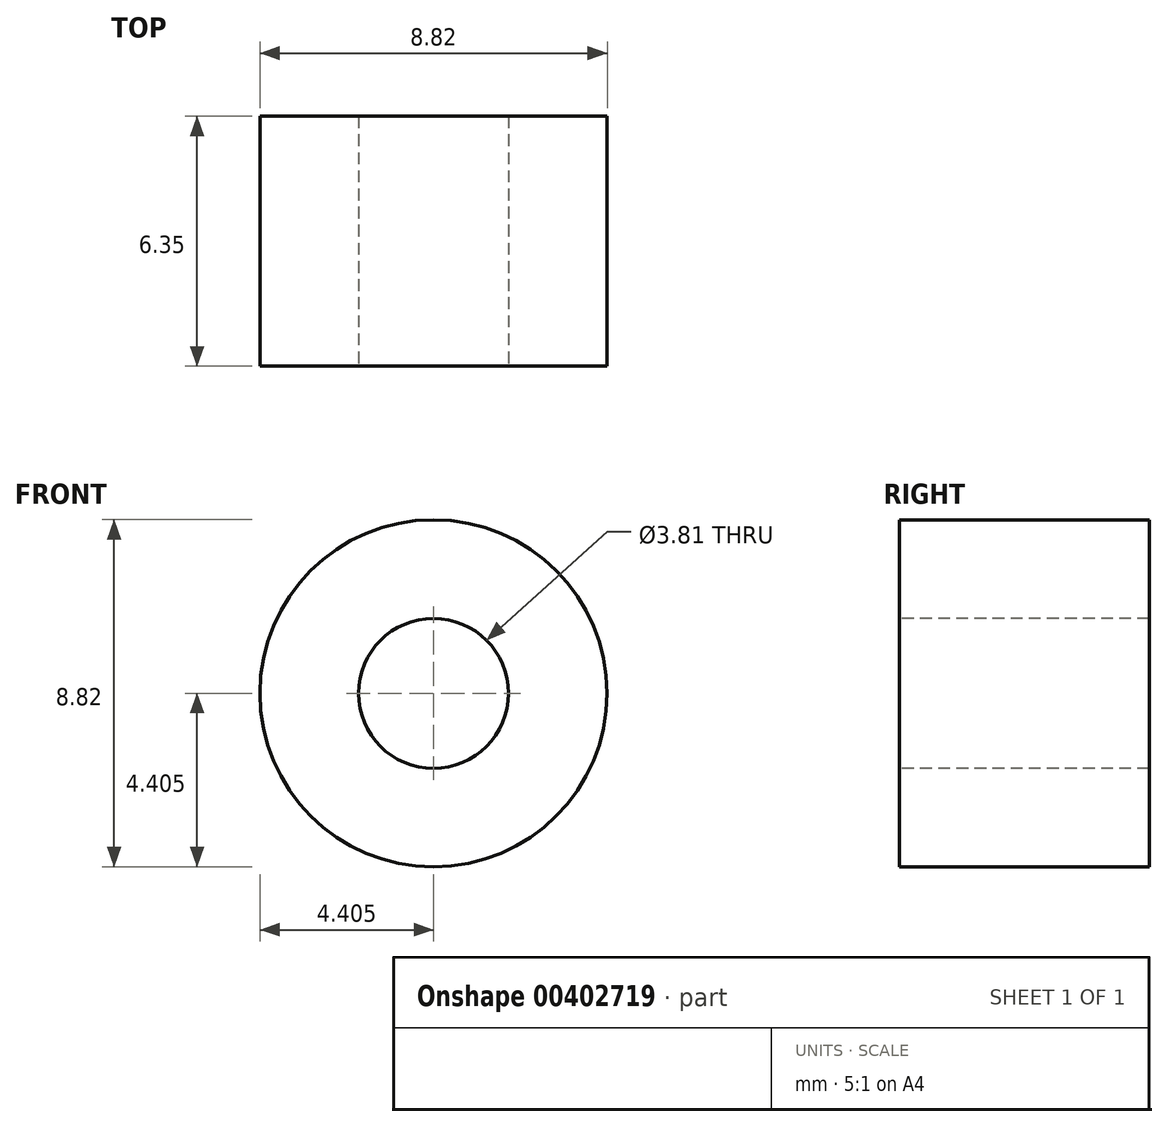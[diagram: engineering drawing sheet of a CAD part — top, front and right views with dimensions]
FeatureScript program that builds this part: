
annotation { "Feature Type Name" : "Feature", "Feature Type Description" : "" }
export const myFeature = defineFeature(function(context is Context, id is Id, definition is map)
    precondition{}
    {
        {
            var Q0;
            Q0=qCreatedBy(makeId("Front.planeOp"),FACE);
            var sketch = newSketch(context, id + "F0", { "sketchPlane" : qUnion([Q0])});
            skCircle(sketch, "E0", {"center": v(-16.21, 58.42) * mm, "radius": 4.4 * mm});
            skSolve(sketch);
        }
        {
            var Q0;
            Q0 = qSketchRegion(id + "F0", true);
            extrude(context, id + "F1", {"entities" : qUnion([Q0]), "oppositeDirection" : true, "depth" : 6.35 * mm});
        }
        {
            var Q0;
            Q0=sQuery(id+"F0.wireOp",VERTEX,"E0.center");
            var Q1;
            Q1=makeQuery(id+"F1.opExtrude","SWEPT_BODY",BODY,{"disambiguationData":[OSD([sQuery(id+"F0.wireOp",EDGE,"E0")])]});
            hole(context, id + "F2", {"style" : HoleStyle.SIMPLE, "endStyle" : HoleEndStyle.THROUGH, "holeDiameter" : 3.8 * mm, "isTappedThrough" : true, "tappedDepth" : 12.7 * mm, "tapClearance" : 3, "locations" : qUnion([Q0]), "scope" : qUnion([Q1])});
        }
    });
